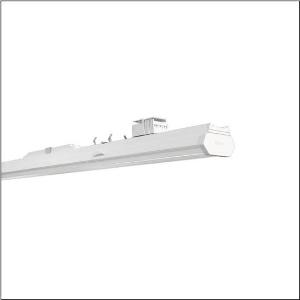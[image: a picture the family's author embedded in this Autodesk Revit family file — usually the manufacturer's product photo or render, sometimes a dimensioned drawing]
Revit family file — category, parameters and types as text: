
# Revit family: licross_r__21_protected_mo_52td1b7n48xg_600d
name_source: partatom
category: Lighting Fixtures
units: mm (PartAtom-declared; Revit-internal decimal feet)

## family parameters
Cut with Voids When Loaded = No
Host = Face
Light Source = No
Part Type = Normal
Room Calculation Point = No
Round Connector Dimension = Use Diameter
Shared = No

## types (1)
- Licross® 21 Protected MO (1 x LED, 8090 lm, 47.9 W, 4000K)
    Apparent Load = 48 VA
    CIE Flux Codes = 54 82 95 97 100
    Color Rendering = 80
    Color Temperature = 4000K
    Default Elevation = 1800 mm
    Description = Licross® 21 Protected MO, luminaire insert, of sheet steel, galvanised, coil coated, white, length: 1.500mm, width: 90mm, height: 103mm, LED rated luminous flux: 8.090lm, light colour: 840, control gear: ON/OFF, with plug, 3-pole, with phase selection, mains connection: 220..240V, AC, 50/60Hz, rated input power: 48W, halogen-free wiring, primary optical cover: cover, of PMMA, light emission: direct distribution, primary light characteristic: symmetric, protection rating (complete): IP54, insulation class (complete): insulation class I (protective earthing), certification: CE, ENEC, VDE, UKCA, protection symbol: D if used in an environment with non-conductive dust loads with corresponding accessories, impact resistance: IK06, permissible ambient temperature for indoor applications: -35..+45°C, corresponds to IFS (International Featured Standards) requirements for safety and quality in the food industry, reducing of maximum allowable ambient temperature of 5°C with ceiling mounting, LABS conformity tested according to VDMA 24364:2018-05, packaging unit: 1 piece
    Height = 92 mm
    Lamp = 1 x LED
    Lamp Light Flux = 8090 lm
    Lamp Power = 47.9 W
    Lamp count = 1
    Length = 1500 mm
    Luminous efficacy = 169 lm/W
    Manufacturer = Siteco
    ModVariant = No
    Model = 52TD1B7N48XG
    Mounting Place = Ceiling
    Mounting Type = Pendant
    Number of Poles = 1
    OnlyDefault = Yes
    Power Factor = 1
    Product Name = Licross® 21 Protected MO
    Product group = luminaire insert
    ProductGroupID = 901
    Protection Class = Protection class I
    Protection Degree = IP 54
    RLX_Detail_Level = 1
    RLX_Emergency_Light_Flux = 0 lm
    RLX_Emergency_Type = 0
    RLX_Emergency_Type_DB = No
    RlxData = <blob elided: 20621 chars, md5=db978376>
    Socket = socket
    Standby Power = 0 W
    System Light Flux = 8090 lm
    System Power = 48 W
    Type Comments = Product without accessories
    Type Image = l_1256148.jpg
    URL = http://relux.com
    VarID = ---
    Voltage = 0 V
    Weight = 0.00 kg
    Width = 88 mm

## geometry (parser evidence)
native form markers: Blend x4, Sweep x11
no freeform markers — native parametric forms only
